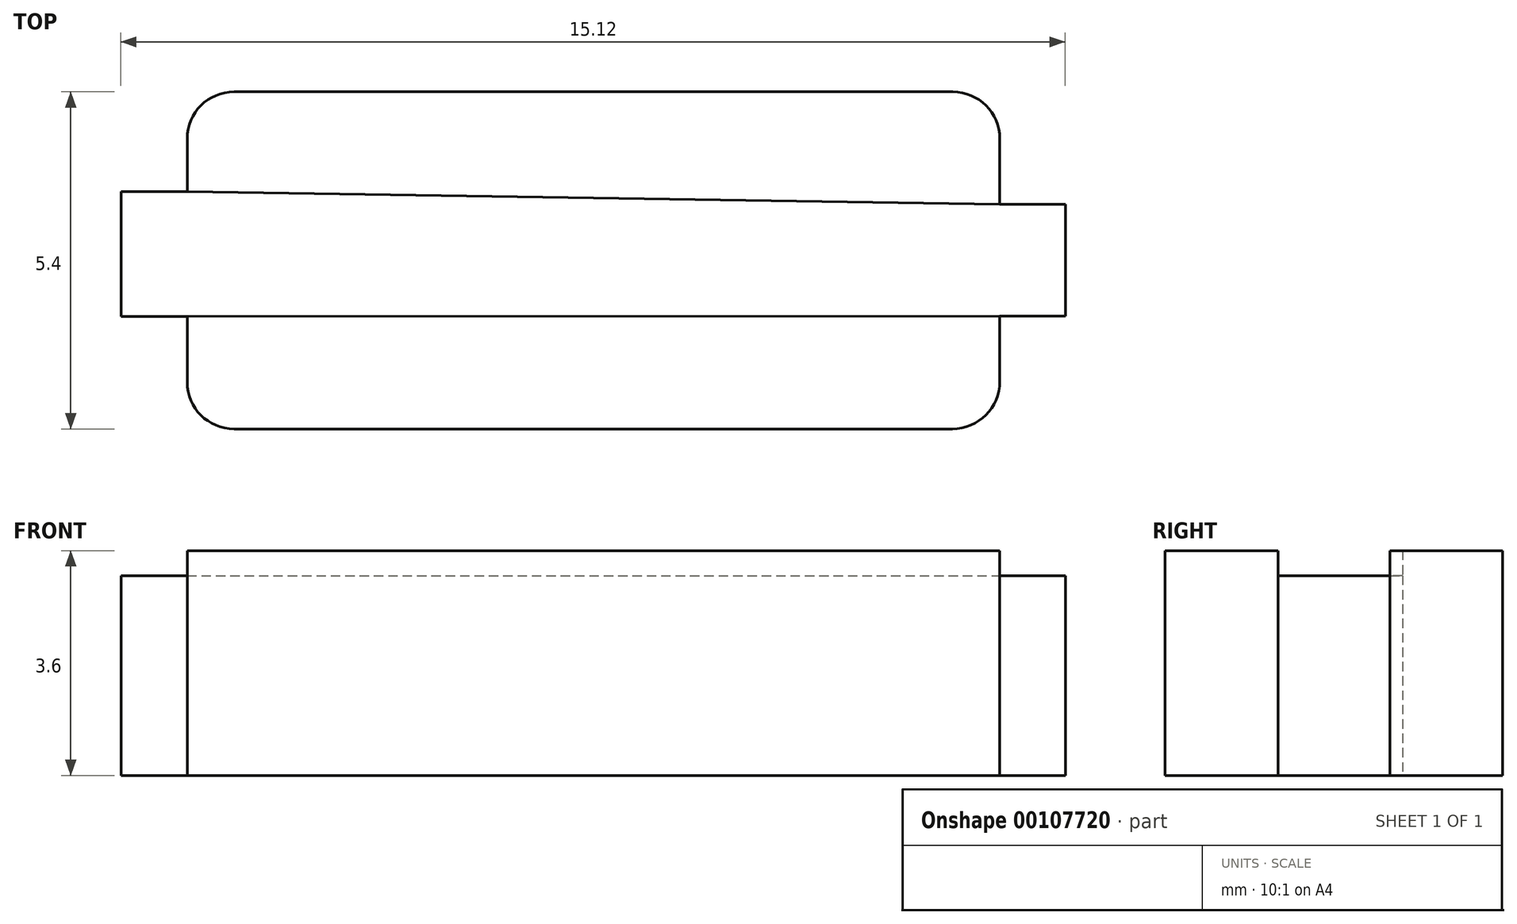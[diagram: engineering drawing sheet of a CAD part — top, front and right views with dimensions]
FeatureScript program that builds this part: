
annotation { "Feature Type Name" : "Feature", "Feature Type Description" : "" }
export const myFeature = defineFeature(function(context is Context, id is Id, definition is map)
    precondition{}
    {
        {
            var Q0;
            Q0=qCreatedBy(makeId("Top.planeOp"),FACE);
            var sketch = newSketch(context, id + "F0", { "sketchPlane" : qUnion([Q0])});
            skLineSegment(sketch, "E0.0", {"start": v(6.35, -0.03) * mm, "end": v(5.3, -0.03) * mm});
            skLineSegment(sketch, "E0.1", {"start": v(6.35, -0.03) * mm, "end": v(6.35, 1.36) * mm});
            skLineSegment(sketch, "E0.2", {"start": v(6.35, 1.36) * mm, "end": v(5.3, 1.36) * mm});
            skLineSegment(sketch, "E0.3", {"start": v(5.3, 2.61) * mm, "end": v(5.3, 1.36) * mm});
            skArc(sketch, "E0.4", {"start": v(5.3, 2.61) * mm, "mid": v(5.14, 3) * mm, "end": v(4.75, 3.16) * mm});
            skLineSegment(sketch, "E0.5", {"start": v(-7.3, -0.04) * mm, "end": v(-7.3, -1.29) * mm});
            skArc(sketch, "E0.6", {"start": v(-7.3, -1.29) * mm, "mid": v(-7.15, -1.68) * mm, "end": v(-6.76, -1.84) * mm});
            skLineSegment(sketch, "E0.7", {"start": v(-6.76, -1.84) * mm, "end": v(4.74, -1.84) * mm});
            skArc(sketch, "E0.8", {"start": v(4.74, -1.84) * mm, "mid": v(5.14, -1.68) * mm, "end": v(5.3, -1.28) * mm});
            skLineSegment(sketch, "E0.9", {"start": v(-8.37, -0.04) * mm, "end": v(-7.3, -0.04) * mm});
            skLineSegment(sketch, "E0.10", {"start": v(-8.37, 1.56) * mm, "end": v(-8.37, -0.04) * mm});
            skLineSegment(sketch, "E0.11", {"start": v(-8.37, 1.56) * mm, "end": v(-7.3, 1.56) * mm});
            skLineSegment(sketch, "E0.12", {"start": v(-7.3, 2.61) * mm, "end": v(-7.3, 1.56) * mm});
            skArc(sketch, "E0.13", {"start": v(-6.76, 3.16) * mm, "mid": v(-7.15, 3) * mm, "end": v(-7.3, 2.61) * mm});
            skLineSegment(sketch, "E0.14", {"start": v(5.3, -0.03) * mm, "end": v(5.3, -1.28) * mm});
            skLineSegment(sketch, "E0.15", {"start": v(-6.76, 3.16) * mm, "end": v(4.75, 3.16) * mm});
            skLineSegment(sketch, "E1", {"start": v(-7.3, -0.04) * mm, "end": v(-7.3, 1.56) * mm});
            skLineSegment(sketch, "E2", {"start": v(5.3, -0.03) * mm, "end": v(5.3, 1.36) * mm});
            skArc(sketch, "E3.0", {"start": v(-6.76, 3.36) * mm, "mid": v(-7.29, 3.14) * mm, "end": v(-7.5, 2.61) * mm});
            skLineSegment(sketch, "E3.1", {"start": v(-7.5, 2.61) * mm, "end": v(-7.5, 1.76) * mm});
            skLineSegment(sketch, "E3.2", {"start": v(-8.57, 1.76) * mm, "end": v(-7.5, 1.76) * mm});
            skLineSegment(sketch, "E3.3", {"start": v(-8.57, 1.76) * mm, "end": v(-8.57, -0.24) * mm});
            skLineSegment(sketch, "E3.4", {"start": v(-8.57, -0.24) * mm, "end": v(-7.5, -0.24) * mm});
            skLineSegment(sketch, "E3.5", {"start": v(6.55, -0.23) * mm, "end": v(6.55, 1.56) * mm});
            skLineSegment(sketch, "E3.6", {"start": v(6.55, 1.56) * mm, "end": v(5.5, 1.56) * mm});
            skLineSegment(sketch, "E3.7", {"start": v(5.5, 2.61) * mm, "end": v(5.5, 1.56) * mm});
            skArc(sketch, "E3.8", {"start": v(5.5, 2.61) * mm, "mid": v(5.28, 3.14) * mm, "end": v(4.75, 3.36) * mm});
            skLineSegment(sketch, "E3.9", {"start": v(6.55, -0.23) * mm, "end": v(5.5, -0.23) * mm});
            skLineSegment(sketch, "E3.10", {"start": v(5.5, -0.23) * mm, "end": v(5.5, -1.28) * mm});
            skArc(sketch, "E3.11", {"start": v(4.74, -2.04) * mm, "mid": v(5.28, -1.82) * mm, "end": v(5.5, -1.28) * mm});
            skLineSegment(sketch, "E3.12", {"start": v(-6.76, -2.04) * mm, "end": v(4.74, -2.04) * mm});
            skArc(sketch, "E3.13", {"start": v(-7.5, -1.29) * mm, "mid": v(-7.29, -1.82) * mm, "end": v(-6.76, -2.04) * mm});
            skLineSegment(sketch, "E3.14", {"start": v(-6.76, 3.36) * mm, "end": v(4.75, 3.36) * mm});
            skLineSegment(sketch, "E3.15", {"start": v(-7.5, -0.24) * mm, "end": v(-7.5, -1.29) * mm});
            skLineSegment(sketch, "E4", {"start": v(-7.5, 1.76) * mm, "end": v(5.5, 1.56) * mm});
            skLineSegment(sketch, "E5", {"start": v(5.5, -0.23) * mm, "end": v(-7.5, -0.24) * mm});
            skSolve(sketch);
        }
        {
            var Q0;
            Q0 = qSketchRegion(id + "F0", true);
            var Q1;
            {var subQ6=sQuery(id+"F0.wireOp",EDGE,"E0.4");Q1=makeQuery(id+"F0.imprint","IMPRINT",FACE,{"disambiguationData":[TD([[makeQuery(id+"F0.imprint","IMPRINT",EDGE,{"derivedFrom":subQ6}),1.0]])]});}
            var Q2;
            Q2=makeQuery(id+"F0.imprint","IMPRINT",FACE,{"disambiguationData":[TD([[makeQuery(id+"F0.imprint","IMPRINT",EDGE,{"derivedFrom":sQuery(id+"F0.wireOp",EDGE,"E0.9")}),1.0]])]});
            var Q3;
            {var subQ4=sQuery(id+"F0.wireOp",EDGE,"E1");Q3=makeQuery(id+"F0.imprint","IMPRINT",FACE,{"disambiguationData":[TD([[makeQuery(id+"F0.imprint","IMPRINT",EDGE,{"derivedFrom":subQ4}),-1.0]])]});}
            var Q4;
            {var subQ1=sQuery(id+"F0.wireOp",EDGE,"E0.6");Q4=makeQuery(id+"F0.imprint","IMPRINT",FACE,{"disambiguationData":[TD([[makeQuery(id+"F0.imprint","IMPRINT",EDGE,{"derivedFrom":subQ1}),1.0]])]});}
            var Q5;
            Q5=makeQuery(id+"F0.imprint","IMPRINT",FACE,{"disambiguationData":[TD([[makeQuery(id+"F0.imprint","IMPRINT",EDGE,{"derivedFrom":sQuery(id+"F0.wireOp",EDGE,"E0.0")}),-1.0]])]});
            extrude(context, id + "F1", {"entities" : qUnion([Q0, Q1, Q2, Q3, Q4, Q5]), "depth" : 3.2 * mm});
        }
        {
            var Q0;
            {var subQ6=sQuery(id+"F0.wireOp",EDGE,"E0.4");Q0=makeQuery(id+"F0.imprint","IMPRINT",FACE,{"disambiguationData":[TD([[makeQuery(id+"F0.imprint","IMPRINT",EDGE,{"derivedFrom":subQ6}),1.0]])]});}
            var Q1;
            {var subQ1=sQuery(id+"F0.wireOp",EDGE,"E0.6");Q1=makeQuery(id+"F0.imprint","IMPRINT",FACE,{"disambiguationData":[TD([[makeQuery(id+"F0.imprint","IMPRINT",EDGE,{"derivedFrom":subQ1}),1.0]])]});}
            var Q2;
            {var subQ5=sQuery(id+"F0.wireOp",EDGE,"E0.6");Q2=makeQuery(id+"F0.imprint","IMPRINT",FACE,{"disambiguationData":[TD([[makeQuery(id+"F0.imprint","IMPRINT",EDGE,{"derivedFrom":subQ5}),-1.0]])]});}
            var Q3;
            {var subQ2=sQuery(id+"F0.wireOp",EDGE,"E0.4");Q3=makeQuery(id+"F0.imprint","IMPRINT",FACE,{"disambiguationData":[TD([[makeQuery(id+"F0.imprint","IMPRINT",EDGE,{"derivedFrom":subQ2}),-1.0]])]});}
            extrude(context, id + "F2", {"entities" : qUnion([Q0, Q1, Q2, Q3]), "operationType" : NewBodyOperationType.ADD, "depth" : 3.6 * mm});
        }
    });
